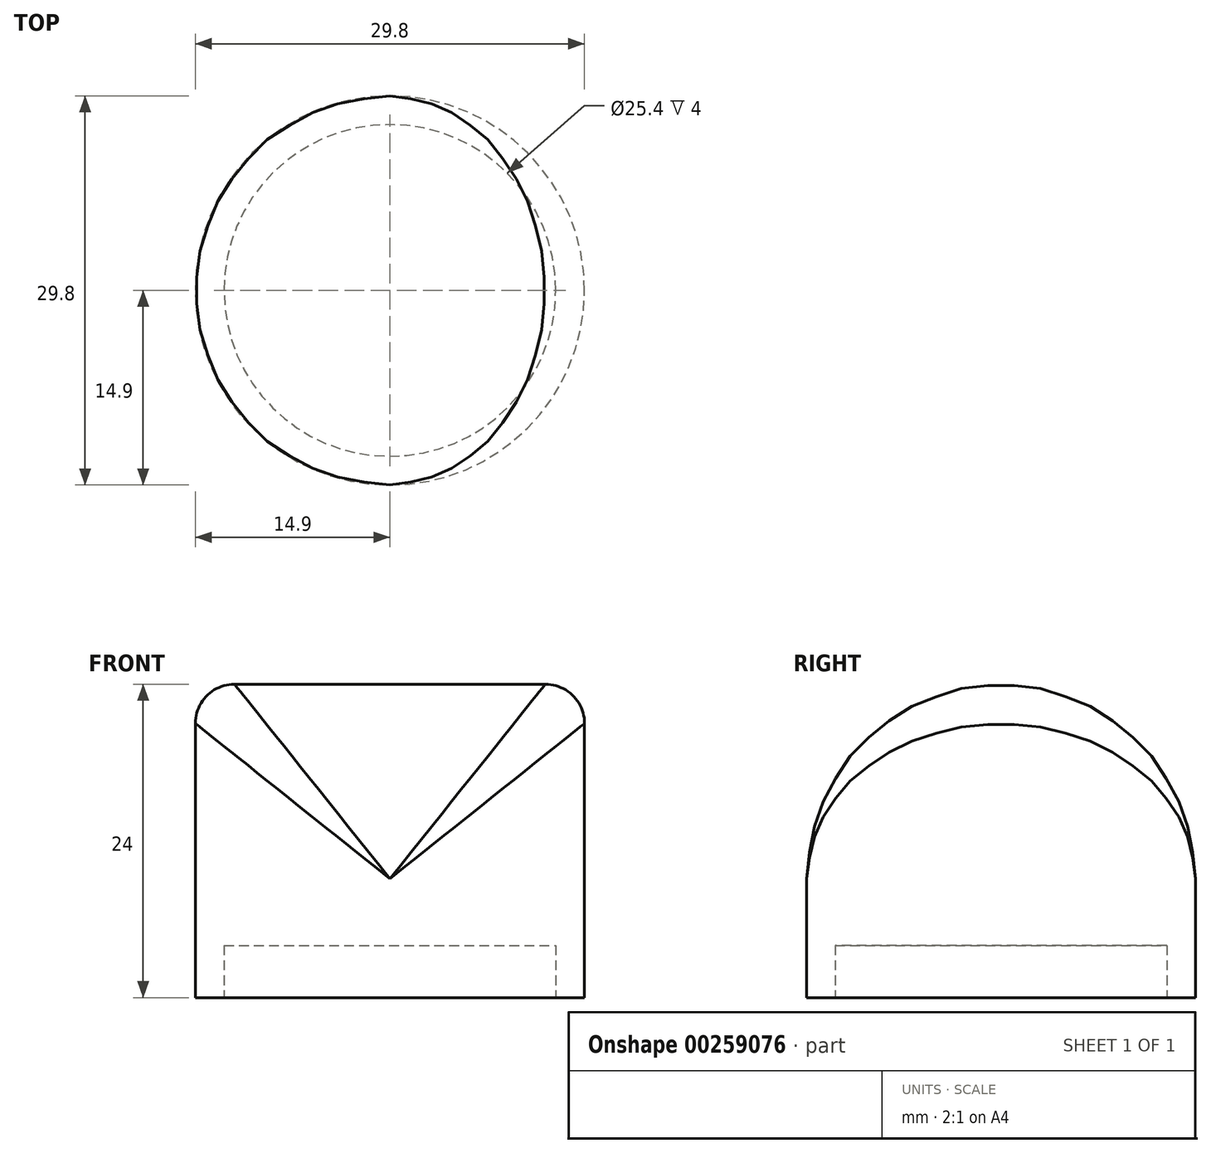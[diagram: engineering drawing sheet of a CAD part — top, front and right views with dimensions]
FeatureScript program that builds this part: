
annotation { "Feature Type Name" : "Feature", "Feature Type Description" : "" }
export const myFeature = defineFeature(function(context is Context, id is Id, definition is map)
    precondition{}
    {
        {
            var Q0;
            Q0=qCreatedBy(makeId("Top.planeOp"),FACE);
            var sketch = newSketch(context, id + "F0", { "sketchPlane" : qUnion([Q0])});
            skCircle(sketch, "E0", {"center": v(0, 0) * mm, "radius": 14.9 * mm});
            skSolve(sketch);
        }
        {
            var Q0;
            Q0=qSketchRegion(id+"F0",true);
            extrude(context, id + "F1", {"entities" : qUnion([Q0]), "depth" : 24 * mm});
        }
        {
            var Q0;
            Q0=makeQuery(id+"F1.opExtrude","CAP_FACE",FACE,{"disambiguationData":[OSD([sQuery(id+"F0.wireOp",EDGE,"E0")])],"isStart":true});
            var sketch = newSketch(context, id + "F2", { "sketchPlane" : qUnion([Q0])});
            skCircle(sketch, "E1", {"center": v(0, 0) * mm, "radius": 12.7 * mm});
            skSolve(sketch);
        }
        {
            var Q0;
            Q0=qSketchRegion(id+"F2",true);
            extrude(context, id + "F3", {"entities" : qUnion([Q0]), "operationType" : NewBodyOperationType.REMOVE, "oppositeDirection" : true, "depth" : 4 * mm});
        }
        {
            var Q0;
            Q0=qCreatedBy(makeId("Right.planeOp"),FACE);
            var sketch = newSketch(context, id + "F4", { "sketchPlane" : qUnion([Q0])});
            skCircle(sketch, "E2", {"center": v(0, 9.1) * mm, "radius": 14.9 * mm});
            skLineSegment(sketch, "E3", {"start": v(0, 9.1) * mm, "end": v(-14.9, 9.1) * mm});
            skLineSegment(sketch, "E4", {"start": v(-14.9, 9.1) * mm, "end": v(-26.5, 19.5) * mm});
            skLineSegment(sketch, "E5", {"start": v(-26.5, 19.5) * mm, "end": v(-22.21, 26.73) * mm});
            skLineSegment(sketch, "E6", {"start": v(-22.21, 26.73) * mm, "end": v(19.76, 27.27) * mm});
            skLineSegment(sketch, "E7", {"start": v(19.76, 27.27) * mm, "end": v(23.24, 9.1) * mm});
            skLineSegment(sketch, "E8", {"start": v(23.24, 9.1) * mm, "end": v(0, 9.1) * mm});
            skSolve(sketch);
        }
        {
            var Q0;
            {var subQ0=sQuery(id+"F4.wireOp",EDGE,"E4");Q0=makeQuery(id+"F4.imprint","IMPRINT",FACE,{"disambiguationData":[TD([[makeQuery(id+"F4.imprint","IMPRINT",EDGE,{"derivedFrom":subQ0}),-1.0]])]});}
            extrude(context, id + "F5", {"entities" : qUnion([Q0]), "operationType" : NewBodyOperationType.REMOVE, "oppositeDirection" : true, "depth" : 25 * mm, "hasSecondDirection" : true, "secondDirectionOppositeDirection" : false, "secondDirectionDepth" : 25 * mm});
        }
        {
            var Q0;
            Q0=makeQuery(id+"F5.boolean.opBoolean","INTERSECT",EDGE,{"disambiguationData":[OD(0.0)],"derivedFrom":[makeQuery(id+"F1.opExtrude","SWEPT_FACE",FACE,{"disambiguationData":[OSD([sQuery(id+"F0.wireOp",EDGE,"E0")])]}),makeQuery(id+"F5.opExtrude","SWEPT_FACE",FACE,{"disambiguationData":[OSD([sQuery(id+"F4.wireOp",EDGE,"E2")])]})]});
            var Q1;
            Q1=makeQuery(id+"F5.boolean.opBoolean","INTERSECT",EDGE,{"disambiguationData":[OD(1.0)],"derivedFrom":[makeQuery(id+"F1.opExtrude","SWEPT_FACE",FACE,{"disambiguationData":[OSD([sQuery(id+"F0.wireOp",EDGE,"E0")])]}),makeQuery(id+"F5.opExtrude","SWEPT_FACE",FACE,{"disambiguationData":[OSD([sQuery(id+"F4.wireOp",EDGE,"E2")])]})]});
            fillet(context, id + "F6", {"entities" : qUnion([Q0, Q1]), "radius" : 3 * mm, "tangentPropagation" : true, "allowEdgeOverflow" : false});
        }
    });
